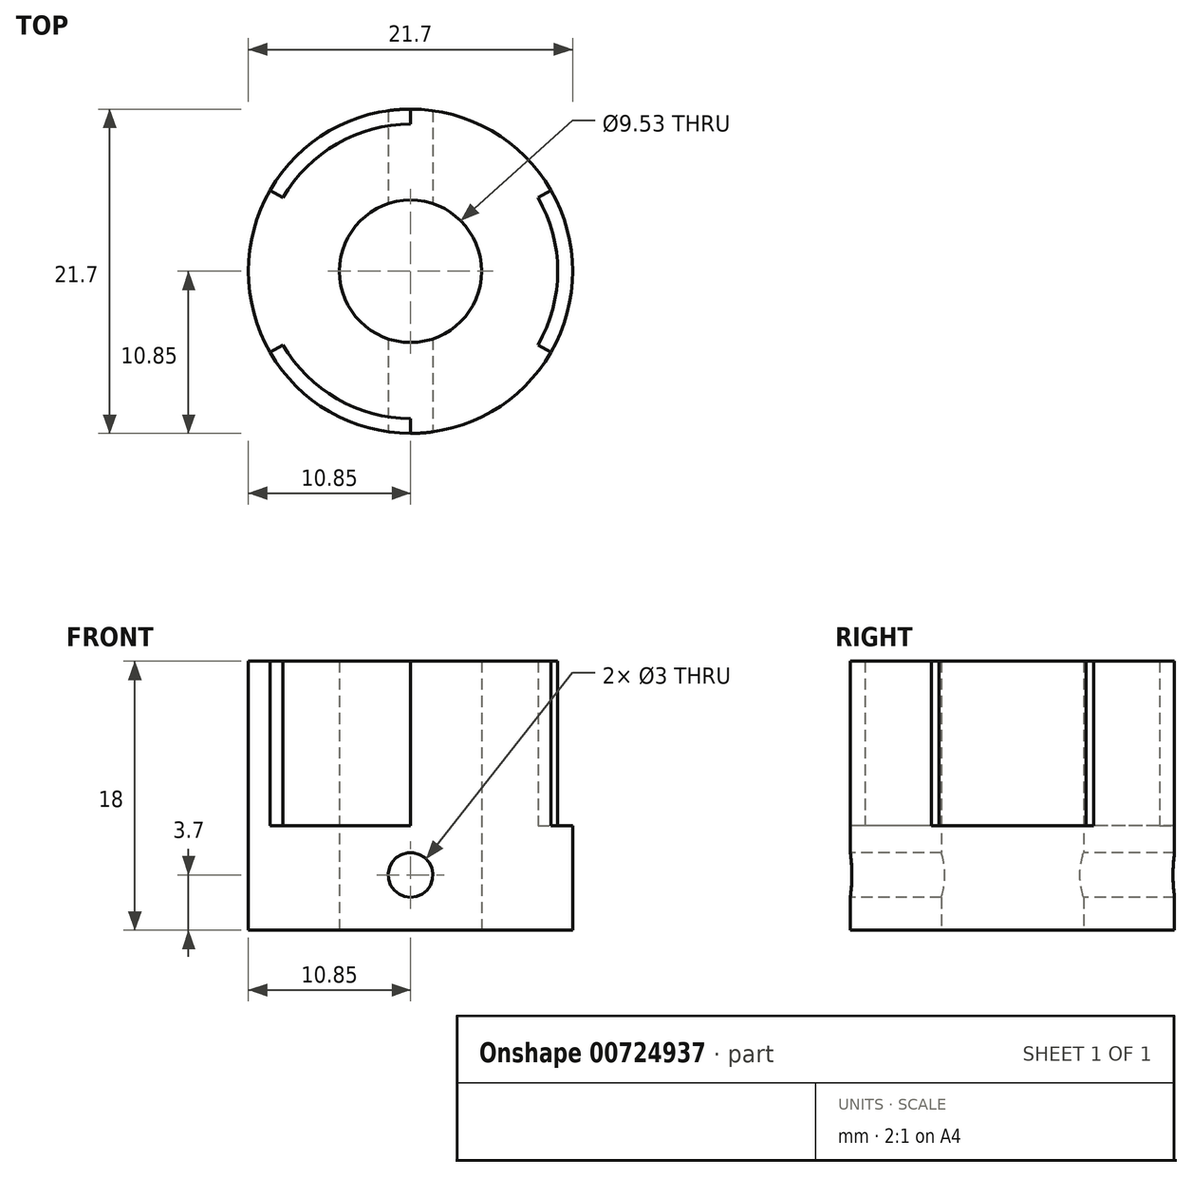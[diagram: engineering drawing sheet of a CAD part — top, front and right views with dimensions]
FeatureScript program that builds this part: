
annotation { "Feature Type Name" : "Feature", "Feature Type Description" : "" }
export const myFeature = defineFeature(function(context is Context, id is Id, definition is map)
    precondition{}
    {
        {
            var Q0;
            Q0=qCreatedBy(makeId("Top.planeOp"),FACE);
            var sketch = newSketch(context, id + "F0", { "sketchPlane" : qUnion([Q0])});
            skArc(sketch, "E0", {"start": v(0, 9.85) * mm, "mid": v(-4.93, 8.53) * mm, "end": v(-8.53, 4.92) * mm});
            skArc(sketch, "E1", {"start": v(-9.4, 5.42) * mm, "mid": v(-10.85, 0) * mm, "end": v(-9.4, -5.43) * mm});
            skLineSegment(sketch, "E2", {"start": v(0, 9.85) * mm, "end": v(0, 10.85) * mm});
            skLineSegment(sketch, "E3.1.0", {"start": v(-8.53, 4.93) * mm, "end": v(-9.4, 5.43) * mm});
            skLineSegment(sketch, "E3.2.0", {"start": v(-8.53, -4.92) * mm, "end": v(-9.4, -5.42) * mm});
            skLineSegment(sketch, "E3.3.0", {"start": v(0, -9.85) * mm, "end": v(0, -10.85) * mm});
            skLineSegment(sketch, "E3.4.0", {"start": v(8.53, -4.93) * mm, "end": v(9.4, -5.43) * mm});
            skLineSegment(sketch, "E3.5.0", {"start": v(8.53, 4.93) * mm, "end": v(9.4, 5.43) * mm});
            skArc(sketch, "E4.trimOffspring", {"start": v(8.53, -4.93) * mm, "mid": v(9.85, 0) * mm, "end": v(8.53, 4.93) * mm});
            skArc(sketch, "E5.trimOffspring", {"start": v(-8.53, -4.92) * mm, "mid": v(-4.92, -8.53) * mm, "end": v(0, -9.85) * mm});
            skArc(sketch, "E6.trimOffspring", {"start": v(0, -10.85) * mm, "mid": v(5.42, -9.4) * mm, "end": v(9.4, -5.43) * mm});
            skArc(sketch, "E7.trimOffspring", {"start": v(9.4, 5.43) * mm, "mid": v(5.42, 9.4) * mm, "end": v(0, 10.85) * mm});
            skCircle(sketch, "E8", {"center": v(0, 0) * mm, "radius": 4.76 * mm});
            skSolve(sketch);
        }
        {
            var Q0;
            Q0=makeQuery(id+"F0.imprint","IMPRINT",FACE,{"disambiguationData":[TD([[makeQuery(id+"F0.imprint","IMPRINT",EDGE,{"derivedFrom":sQuery(id+"F0.wireOp",EDGE,"E0")}),1.0]])]});
            extrude(context, id + "F1", {"entities" : qUnion([Q0]), "depth" : 18 * mm, "offsetDistance" : 25 * mm});
        }
        {
            var Q0;
            Q0=qCreatedBy(makeId("Top.planeOp"),FACE);
            var sketch = newSketch(context, id + "F2", { "sketchPlane" : qUnion([Q0])});
            skCircle(sketch, "E9", {"center": v(0, 0) * mm, "radius": 10.85 * mm});
            skCircle(sketch, "E10", {"center": v(0, 0) * mm, "radius": 4.76 * mm});
            skSolve(sketch);
        }
        {
            var Q0;
            Q0=makeQuery(id+"F2.imprint","IMPRINT",FACE,{"disambiguationData":[TD([[makeQuery(id+"F2.imprint","IMPRINT",EDGE,{"derivedFrom":sQuery(id+"F2.wireOp",EDGE,"E9")}),1.0]])]});
            extrude(context, id + "F3", {"entities" : qUnion([Q0]), "operationType" : NewBodyOperationType.ADD, "depth" : 7 * mm, "offsetDistance" : 25 * mm});
        }
        {
            var Q0;
            Q0=qCreatedBy(makeId("Front.planeOp"),FACE);
            var sketch = newSketch(context, id + "F4", { "sketchPlane" : qUnion([Q0])});
            skCircle(sketch, "E11", {"center": v(0, 3.7) * mm, "radius": 1.5 * mm});
            skSolve(sketch);
        }
        {
            var Q0;
            Q0=qSketchRegion(id+"F4",true);
            extrude(context, id + "F5", {"entities" : qUnion([Q0]), "operationType" : NewBodyOperationType.REMOVE, "endBound" : BoundingType.SYMMETRIC, "oppositeDirection" : true, "depth" : 25 * mm, "offsetDistance" : 25 * mm});
        }
    });
